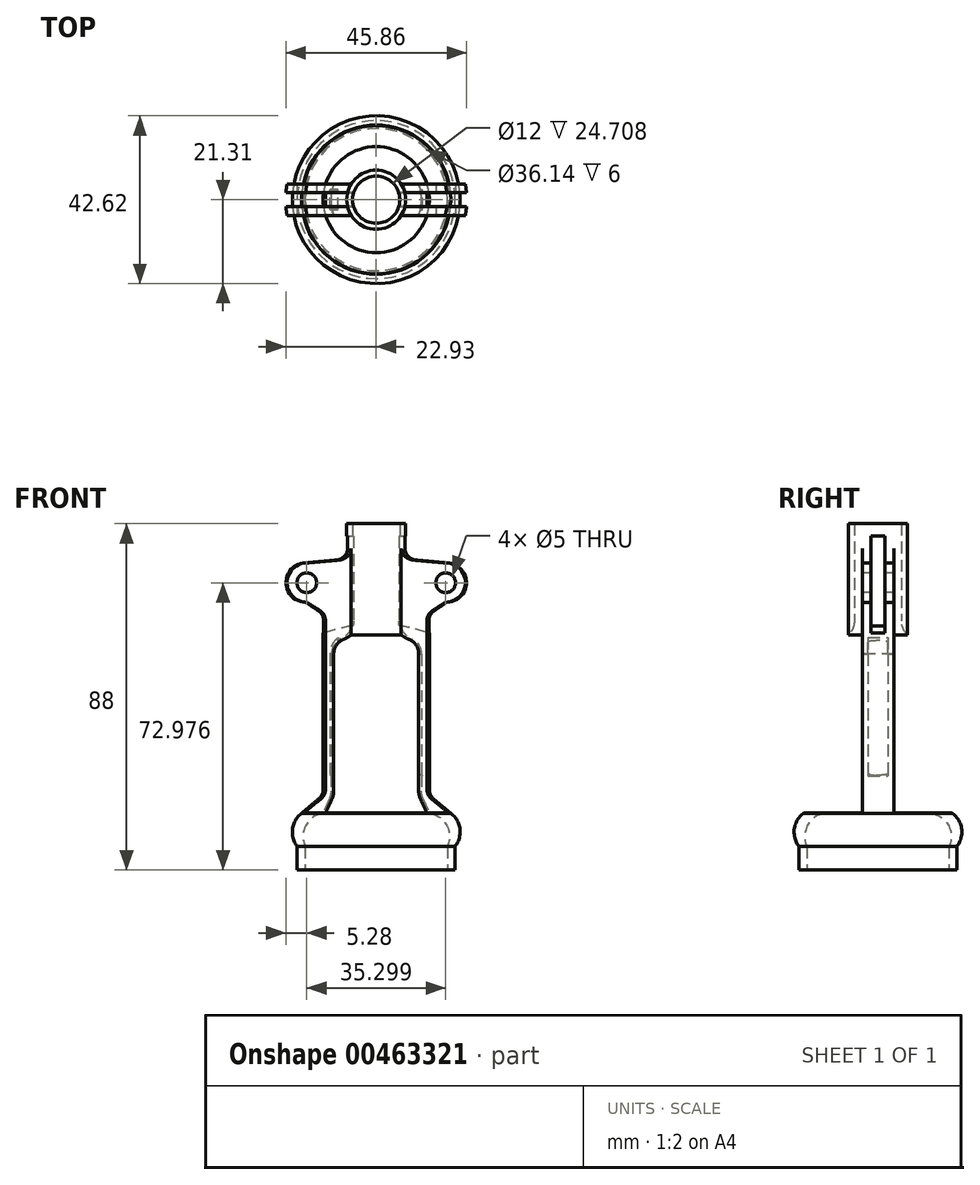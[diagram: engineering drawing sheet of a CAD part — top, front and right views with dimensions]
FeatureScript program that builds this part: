
annotation { "Feature Type Name" : "Feature", "Feature Type Description" : "" }
export const myFeature = defineFeature(function(context is Context, id is Id, definition is map)
    precondition{}
    {
        {
            var Q0;
            Q0=qCreatedBy(makeId("Front.planeOp"),FACE);
            var sketch = newSketch(context, id + "F0", { "sketchPlane" : qUnion([Q0])});
            skLineSegment(sketch, "E0", {"start": v(0, -8.92) * mm, "end": v(0, 135.5) * mm, "construction": true});
            skLineSegment(sketch, "E1", {"start": v(0, 88) * mm, "end": v(6, 88) * mm});
            skLineSegment(sketch, "E2", {"start": v(0, 0) * mm, "end": v(0, 88) * mm});
            skLineSegment(sketch, "E3", {"start": v(6, 88) * mm, "end": v(7.5, 88) * mm});
            skLineSegment(sketch, "E4", {"start": v(7.5, 88) * mm, "end": v(7.5, 79) * mm});
            skLineSegment(sketch, "E5", {"start": v(6, 88) * mm, "end": v(6, 59) * mm});
            skLineSegment(sketch, "E6", {"start": v(7.5, 79) * mm, "end": v(18, 78) * mm});
            skCircle(sketch, "E7", {"center": v(18, 73) * mm, "radius": 5 * mm});
            skLineSegment(sketch, "E8", {"start": v(18, 68) * mm, "end": v(13.5, 65) * mm});
            skLineSegment(sketch, "E9", {"start": v(13.5, 65) * mm, "end": v(13.5, 19) * mm});
            skLineSegment(sketch, "E10", {"start": v(6, 59) * mm, "end": v(7.5, 59) * mm});
            skArc(sketch, "E11", {"start": v(11.5, 54.87) * mm, "mid": v(10.37, 57.78) * mm, "end": v(7.5, 59) * mm});
            skLineSegment(sketch, "E12", {"start": v(11.5, 54.87) * mm, "end": v(11.5, 19) * mm});
            skLineSegment(sketch, "E13", {"start": v(0, 0) * mm, "end": v(20.07, 0) * mm});
            skLineSegment(sketch, "E14", {"start": v(11.5, 19) * mm, "end": v(13.5, 14.42) * mm});
            skLineSegment(sketch, "E15", {"start": v(13.5, 19) * mm, "end": v(18.95, 14.42) * mm});
            skLineSegment(sketch, "E16", {"start": v(20.07, 0) * mm, "end": v(20.07, 6) * mm});
            skLineSegment(sketch, "E17", {"start": v(20.07, 0) * mm, "end": v(18.07, 0) * mm});
            skLineSegment(sketch, "E18", {"start": v(18.07, 0) * mm, "end": v(18.07, 6) * mm});
            skArc(sketch, "E19", {"start": v(20.07, 6) * mm, "mid": v(21.26, 10.44) * mm, "end": v(18.95, 14.42) * mm});
            skArc(sketch, "E20", {"start": v(18.07, 6) * mm, "mid": v(17.88, 11.35) * mm, "end": v(13.5, 14.42) * mm});
            skSolve(sketch);
        }
        {
            var Q0;
            Q0=makeQuery(id+"F0.imprint","IMPRINT",FACE,{"disambiguationData":[TD([[makeQuery(id+"F0.imprint","IMPRINT",EDGE,{"derivedFrom":sQuery(id+"F0.wireOp",EDGE,"E3")}),-1.0]])]});
            var Q1;
            {var subQ0=sQuery(id+"F0.wireOp",EDGE,"E7");var subQ1=makeQuery(id+"F0.imprint","INTERSECT",VERTEX,{"derivedFrom":[sQuery(id+"F0.wireOp",EDGE,"E6"),subQ0]});Q1=makeQuery(id+"F0.imprint","IMPRINT",FACE,{"disambiguationData":[TD([[makeQuery(id+"F0.imprint","IMPRINT",EDGE,{"disambiguationData":[TD([[subQ1,-1.0]])],"derivedFrom":subQ0}),1.0]])]});}
            var Q2;
            Q2=sQuery(id+"F0.wireOp",EDGE,"E2");
            revolve(context, id + "F1", {"entities" : qUnion([Q0, Q1]), "axis" : qUnion([Q2]), "revolveType" : RevolveType.FULL});
        }
        {
            var Q0;
            Q0=makeQuery(id+"F1.opRevolve","SWEPT_EDGE",EDGE,{"disambiguationData":[OSD([sQuery(id+"F0.wireOp",EDGE,"E4"),sQuery(id+"F0.wireOp",EDGE,"E6")])]});
            var Q1;
            Q1=makeQuery(id+"F1.opRevolve","SWEPT_EDGE",EDGE,{"disambiguationData":[OSD([sQuery(id+"F0.wireOp",EDGE,"E8"),sQuery(id+"F0.wireOp",EDGE,"E9")])]});
            var Q2;
            Q2=makeQuery(id+"F1.opRevolve","SWEPT_EDGE",EDGE,{"disambiguationData":[OSD([sQuery(id+"F0.wireOp",EDGE,"E9"),sQuery(id+"F0.wireOp",EDGE,"E15")])]});
            fillet(context, id + "F2", {"entities" : qUnion([Q0, Q1, Q2]), "radius" : 3 * mm, "tangentPropagation" : true, "allowEdgeOverflow" : false});
        }
        {
            var Q0;
            Q0=makeQuery(id+"F1.opRevolve","SWEPT_EDGE",EDGE,{"disambiguationData":[OSD([sQuery(id+"F0.wireOp",EDGE,"E5"),sQuery(id+"F0.wireOp",EDGE,"E10")])]});
            var Q1;
            Q1=makeQuery(id+"F1.opRevolve","SWEPT_EDGE",EDGE,{"disambiguationData":[OSD([sQuery(id+"F0.wireOp",EDGE,"E12"),sQuery(id+"F0.wireOp",EDGE,"E14")])]});
            fillet(context, id + "F3", {"entities" : qUnion([Q0, Q1]), "radius" : 5 * mm, "tangentPropagation" : true, "allowEdgeOverflow" : false});
        }
        {
            var Q0;
            Q0=makeQuery(id+"F1.opRevolve","SWEPT_FACE",FACE,{"disambiguationData":[OSD([sQuery(id+"F0.wireOp",EDGE,"E3")])]});
            var sketch = newSketch(context, id + "F4", { "sketchPlane" : qUnion([Q0])});
            skLineSegment(sketch, "E21", {"start": v(-28.84, 0) * mm, "end": v(27.21, 0) * mm, "construction": true});
            skLineSegment(sketch, "E22", {"start": v(-22.83, 4) * mm, "end": v(-6.34, 4) * mm});
            skLineSegment(sketch, "E23.MirrorCS", {"start": v(-22.83, -4) * mm, "end": v(-6.34, -4) * mm});
            skPoint(sketch, "E24", {"position": v(-6.34, 4) * mm});
            skPoint(sketch, "E25", {"position": v(6.34, 4) * mm});
            skLineSegment(sketch, "E26.trimOffspring", {"start": v(6.34, 4) * mm, "end": v(22.83, 4) * mm});
            skPoint(sketch, "E27", {"position": v(-6.34, -4) * mm});
            skPoint(sketch, "E28", {"position": v(6.34, -4) * mm});
            skLineSegment(sketch, "E29.trimOffspring", {"start": v(6.34, -4) * mm, "end": v(22.83, -4) * mm});
            skCircle(sketch, "E30", {"center": v(0, 0) * mm, "radius": 23.18 * mm});
            skSolve(sketch);
        }
        {
            var Q0;
            {var subQ0=sQuery(id+"F4.wireOp",EDGE,"E22");Q0=makeQuery(id+"F4.imprint","IMPRINT",FACE,{"disambiguationData":[TD([[makeQuery(id+"F4.imprint","IMPRINT",EDGE,{"derivedFrom":subQ0}),1.0]])]});}
            var Q1;
            {var subQ0=sQuery(id+"F4.wireOp",EDGE,"E23.MirrorCS");Q1=makeQuery(id+"F4.imprint","IMPRINT",FACE,{"disambiguationData":[TD([[makeQuery(id+"F4.imprint","IMPRINT",EDGE,{"derivedFrom":subQ0}),-1.0]])]});}
            extrude(context, id + "F5", {"entities" : qUnion([Q0, Q1]), "operationType" : NewBodyOperationType.REMOVE, "oppositeDirection" : true, "depth" : 73.5 * mm});
        }
        {
            var Q0;
            Q0=qCreatedBy(makeId("Front.planeOp"),FACE);
            var sketch = newSketch(context, id + "F6", { "sketchPlane" : qUnion([Q0])});
            skLineSegment(sketch, "E31", {"start": v(0, 52.34) * mm, "end": v(0, 101.38) * mm, "construction": true});
            skLineSegment(sketch, "E32", {"start": v(0, 84.86) * mm, "end": v(27.37, 84.86) * mm});
            skLineSegment(sketch, "E33", {"start": v(27.37, 84.86) * mm, "end": v(27.37, 60.27) * mm});
            skLineSegment(sketch, "E34", {"start": v(27.37, 60.27) * mm, "end": v(12.9, 60.27) * mm});
            skArc(sketch, "E35", {"start": v(12.9, 60.27) * mm, "mid": v(6.55, 61.92) * mm, "end": v(0, 62.23) * mm});
            skLineSegment(sketch, "E36.MirrorCS", {"start": v(-27.37, 60.27) * mm, "end": v(-12.9, 60.27) * mm});
            skLineSegment(sketch, "E37.MirrorCS", {"start": v(-27.37, 84.86) * mm, "end": v(-27.37, 60.27) * mm});
            skArc(sketch, "E38.MirrorCS", {"start": v(-12.9, 60.27) * mm, "mid": v(-6.55, 61.92) * mm, "end": v(0, 62.23) * mm});
            skLineSegment(sketch, "E39.MirrorCS", {"start": v(0, 84.86) * mm, "end": v(-27.37, 84.86) * mm});
            skSolve(sketch);
        }
        {
            var Q0;
            Q0 = qSketchRegion(id + "F6", true);
            extrude(context, id + "F7", {"entities" : qUnion([Q0]), "operationType" : NewBodyOperationType.REMOVE, "endBound" : BoundingType.SYMMETRIC, "oppositeDirection" : true, "depth" : 3.5 * mm});
        }
        {
            var Q0;
            Q0=qCreatedBy(makeId("Front.planeOp"),FACE);
            var sketch = newSketch(context, id + "F8", { "sketchPlane" : qUnion([Q0])});
            skFitSpline(sketch, "E40.0", {"points": [v(8.5, 59.62) * mm, v(8.36, 59.67) * mm, v(8.09, 59.79) * mm, v(7.58, 60.06) * mm, v(7.22, 60.3) * mm, v(7, 60.49) * mm]});
            skFitSpline(sketch, "E40.1", {"points": [v(8.5, 59.62) * mm, v(8.73, 59.53) * mm, v(9.19, 59.32) * mm, v(9.84, 58.9) * mm, v(10.32, 58.48) * mm, v(10.66, 58.1) * mm, v(10.98, 57.68) * mm, v(11.32, 57.12) * mm, v(11.6, 56.4) * mm, v(11.77, 55.62) * mm, v(11.8, 55.1) * mm, v(11.79, 54.83) * mm]});
            skLineSegment(sketch, "E40.2", {"start": v(11.78, 20.04) * mm, "end": v(11.78, 54.85) * mm});
            skLineSegment(sketch, "E41", {"start": v(9.63, 59.02) * mm, "end": v(9.63, 27.96) * mm});
            skArc(sketch, "E42", {"start": v(9.63, 27.96) * mm, "mid": v(10.2, 25.64) * mm, "end": v(11.78, 23.85) * mm});
            skLineSegment(sketch, "E43", {"start": v(11.78, 54.85) * mm, "end": v(11.78, 20.04) * mm});
            skLineSegment(sketch, "E44", {"start": v(0, 107.12) * mm, "end": v(0, -12.22) * mm, "construction": true});
            skLineSegment(sketch, "E45.MirrorCS", {"start": v(-9.63, 59.02) * mm, "end": v(-9.63, 27.96) * mm});
            skLineSegment(sketch, "E46.MirrorCS", {"start": v(-11.78, 54.85) * mm, "end": v(-11.78, 20.04) * mm});
            skArc(sketch, "E47.MirrorCS", {"start": v(-9.63, 27.96) * mm, "mid": v(-10.2, 25.64) * mm, "end": v(-11.78, 23.85) * mm});
            skArc(sketch, "E48", {"start": v(-9.63, 59.02) * mm, "mid": v(-11.21, 57.2) * mm, "end": v(-11.78, 54.85) * mm});
            skSolve(sketch);
        }
        {
            var Q0;
            Q0 = qSketchRegion(id + "F8", true);
            extrude(context, id + "F9", {"entities" : qUnion([Q0]), "operationType" : NewBodyOperationType.REMOVE, "endBound" : BoundingType.SYMMETRIC, "depth" : 5 * mm});
        }
        {
            var Q0;
            Q0=makeQuery(id+"F5.boolean.opBoolean","COPY",FACE,{"derivedFrom":makeQuery(id+"F5.opExtrude","SWEPT_FACE",FACE,{"disambiguationData":[OSD([sQuery(id+"F4.wireOp",EDGE,"E29.trimOffspring")])]})});
            var sketch = newSketch(context, id + "F10", { "sketchPlane" : qUnion([Q0])});
            skCircle(sketch, "E49", {"center": v(17.65, 72.98) * mm, "radius": 2.5 * mm});
            skCircle(sketch, "E50.MirrorC", {"center": v(-17.65, 72.98) * mm, "radius": 2.5 * mm});
            skSolve(sketch);
        }
        {
            var Q0;
            Q0 = qSketchRegion(id + "F10", true);
            extrude(context, id + "F11", {"entities" : qUnion([Q0]), "operationType" : NewBodyOperationType.REMOVE, "endBound" : BoundingType.THROUGH_ALL, "oppositeDirection" : true, "depth" : 25 * mm});
        }
    });
